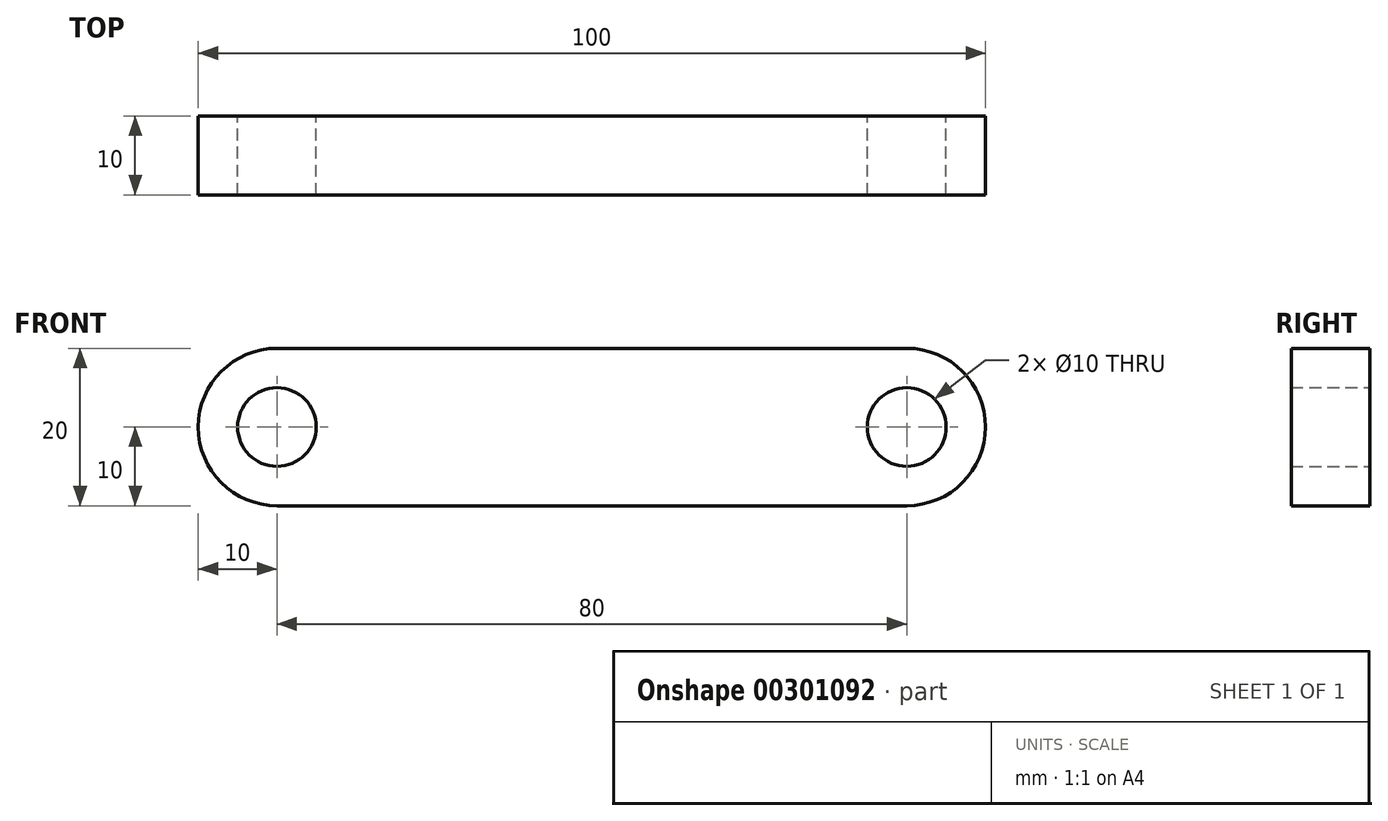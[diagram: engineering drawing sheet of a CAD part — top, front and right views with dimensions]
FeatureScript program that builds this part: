
annotation { "Feature Type Name" : "Feature", "Feature Type Description" : "" }
export const myFeature = defineFeature(function(context is Context, id is Id, definition is map)
    precondition{}
    {
        {
            var Q0;
            Q0=qCreatedBy(makeId("Front.planeOp"),FACE);
            var sketch = newSketch(context, id + "F0", { "sketchPlane" : qUnion([Q0])});
            skLineSegment(sketch, "E0", {"start": v(0, 0) * mm, "end": v(80, 0) * mm});
            skLineSegment(sketch, "E1", {"start": v(0, 20) * mm, "end": v(80, 20) * mm});
            skArc(sketch, "E2", {"start": v(0, 20) * mm, "mid": v(-10, 10) * mm, "end": v(0, 0) * mm});
            skArc(sketch, "E3", {"start": v(80, 20) * mm, "mid": v(90, 10) * mm, "end": v(80, 0) * mm});
            skCircle(sketch, "E4", {"center": v(0, 10) * mm, "radius": 5 * mm});
            skCircle(sketch, "E5", {"center": v(80, 10) * mm, "radius": 5 * mm});
            skSolve(sketch);
        }
        {
            var Q0;
            Q0 = qSketchRegion(id + "F0", true);
            extrude(context, id + "F1", {"entities" : qUnion([Q0]), "depth" : 10 * mm});
        }
    });
